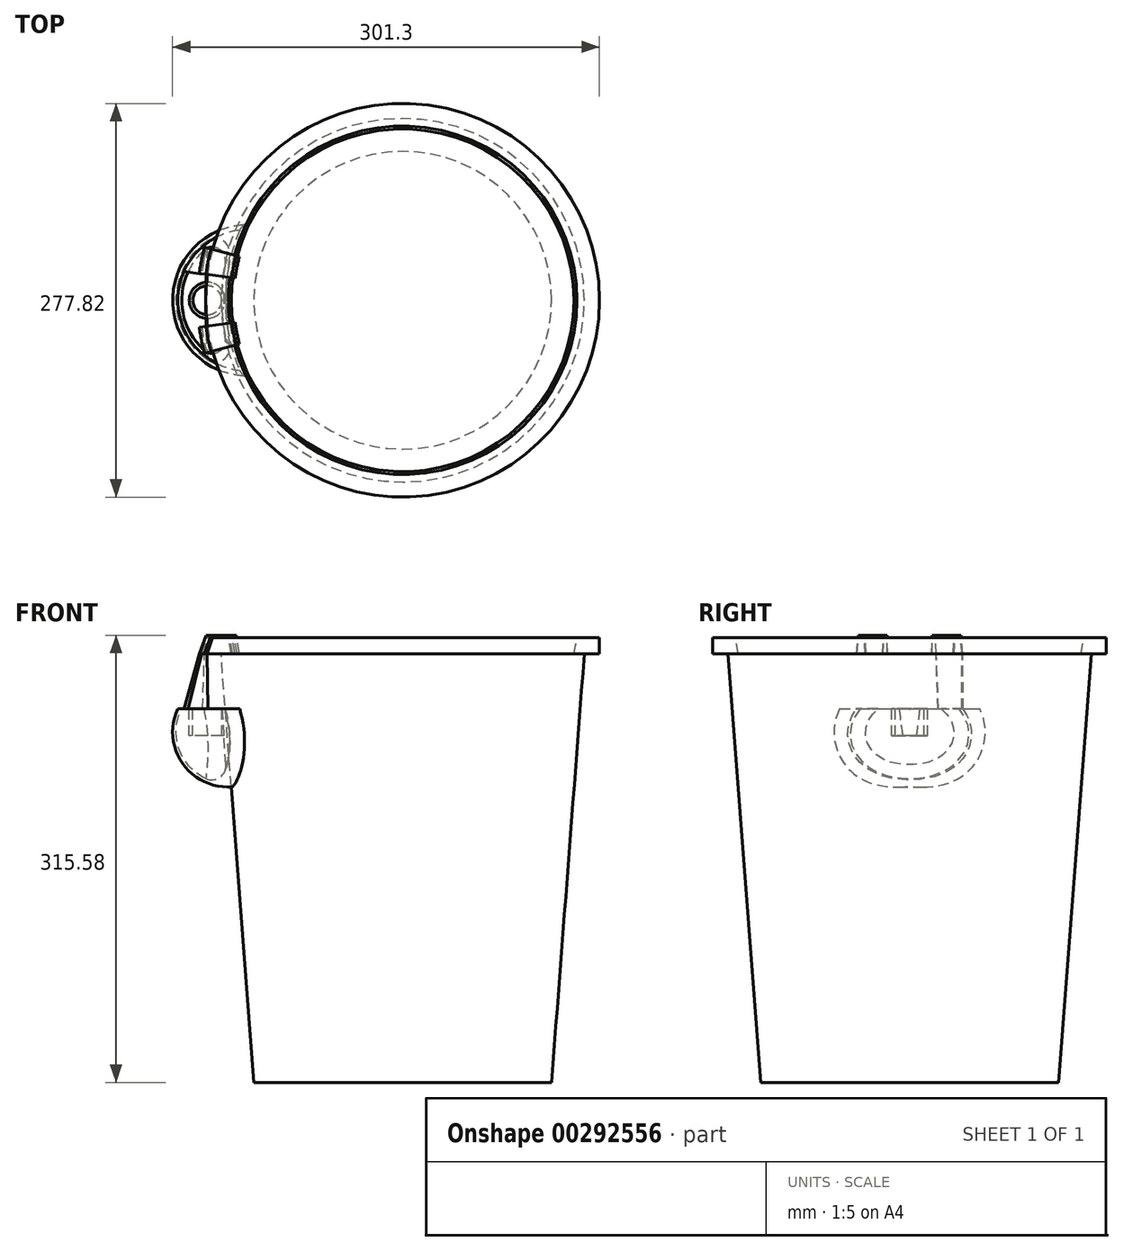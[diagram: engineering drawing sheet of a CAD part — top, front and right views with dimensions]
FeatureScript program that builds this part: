
annotation { "Feature Type Name" : "Feature", "Feature Type Description" : "" }
export const myFeature = defineFeature(function(context is Context, id is Id, definition is map)
    precondition{}
    {
        {
            var Q0;
            Q0=qCreatedBy(makeId("Front.planeOp"),FACE);
            var sketch = newSketch(context, id + "F0", { "sketchPlane" : qUnion([Q0])});
            skLineSegment(sketch, "E0", {"start": v(0, 0) * mm, "end": v(-105.1, 0) * mm});
            skLineSegment(sketch, "E1", {"start": v(-105.1, 0) * mm, "end": v(-128.2, 302.33) * mm});
            skLineSegment(sketch, "E2", {"start": v(-128.2, 302.33) * mm, "end": v(0, 302.33) * mm});
            skLineSegment(sketch, "E3", {"start": v(0, 302.33) * mm, "end": v(0, 0) * mm});
            skLineSegment(sketch, "E4.MirrorCS", {"start": v(128.2, 302.33) * mm, "end": v(0, 302.33) * mm, "construction": true});
            skLineSegment(sketch, "E5.MirrorCS", {"start": v(105.1, 0) * mm, "end": v(128.2, 302.33) * mm});
            skLineSegment(sketch, "E6.MirrorCS", {"start": v(0, 0) * mm, "end": v(105.1, 0) * mm});
            skArc(sketch, "E7", {"start": v(-138.8, 282.91) * mm, "mid": v(-150.57, 275.12) * mm, "end": v(-158.77, 263.61) * mm});
            skLineSegment(sketch, "E8", {"start": v(-125.23, 263.61) * mm, "end": v(-158.77, 263.61) * mm});
            skArc(sketch, "E9", {"start": v(-158.77, 263.61) * mm, "mid": v(-155.6, 225.36) * mm, "end": v(-121.04, 208.66) * mm});
            skLineSegment(sketch, "E10", {"start": v(-121.04, 208.66) * mm, "end": v(-121.04, 269.89) * mm, "construction": true});
            skLineSegment(sketch, "E11", {"start": v(-108.91, 147.35) * mm, "end": v(-108.91, 247.43) * mm});
            skLineSegment(sketch, "E12.bottom", {"start": v(-120.9, 302.33) * mm, "end": v(-138.9, 302.33) * mm});
            skLineSegment(sketch, "E12.top", {"start": v(-123, 313.98) * mm, "end": v(-138.9, 313.98) * mm});
            skLineSegment(sketch, "E12.left", {"start": v(-120.9, 302.33) * mm, "end": v(-123, 313.98) * mm});
            skLineSegment(sketch, "E12.right", {"start": v(-138.9, 302.33) * mm, "end": v(-138.9, 313.98) * mm});
            skLineSegment(sketch, "E13.MirrorCS", {"start": v(120.9, 302.33) * mm, "end": v(123, 313.98) * mm});
            skLineSegment(sketch, "E14.MirrorCS", {"start": v(123, 313.98) * mm, "end": v(138.9, 313.98) * mm});
            skLineSegment(sketch, "E15.MirrorCS", {"start": v(138.9, 302.33) * mm, "end": v(138.9, 313.98) * mm});
            skLineSegment(sketch, "E16.MirrorCS", {"start": v(120.9, 302.33) * mm, "end": v(138.9, 302.33) * mm});
            skSolve(sketch);
        }
        {
            var Q0;
            {var subQ4=sQuery(id+"F0.wireOp",EDGE,"E0");Q0=makeQuery(id+"F0.imprint","IMPRINT",FACE,{"disambiguationData":[TD([[makeQuery(id+"F0.imprint","IMPRINT",EDGE,{"derivedFrom":subQ4}),-1.0]])]});}
            var Q1;
            Q1=makeQuery(id+"F0.imprint","IMPRINT",FACE,{"disambiguationData":[TD([[makeQuery(id+"F0.imprint","IMPRINT",EDGE,{"derivedFrom":sQuery(id+"F0.wireOp",EDGE,"E12.top")}),1.0]])]});
            var Q2;
            Q2=sQuery(id+"F0.wireOp",EDGE,"E3");
            revolve(context, id + "F1", {"entities" : qUnion([Q0, Q1]), "axis" : qUnion([Q2]), "revolveType" : RevolveType.FULL});
        }
        {
            var Q0;
            {var subQ0=sQuery(id+"F0.wireOp",EDGE,"E8");Q0=makeQuery(id+"F0.imprint","IMPRINT",FACE,{"disambiguationData":[TD([[makeQuery(id+"F0.imprint","IMPRINT",EDGE,{"derivedFrom":subQ0}),1.0]])]});}
            var Q1;
            Q1=sQuery(id+"F0.wireOp",EDGE,"E11");
            revolve(context, id + "F2", {"entities" : qUnion([Q0]), "axis" : qUnion([Q1]), "revolveType" : RevolveType.FULL});
        }
        {
            var Q0;
            Q0=makeQuery(id+"F1.opRevolve","SWEPT_BODY",BODY,{"disambiguationData":[OSD([sQuery(id+"F0.wireOp",EDGE,"E0"),sQuery(id+"F0.wireOp",EDGE,"E1"),sQuery(id+"F0.wireOp",EDGE,"E2"),sQuery(id+"F0.wireOp",EDGE,"E3")])]});
            var Q1;
            Q1=makeQuery(id+"F2.opRevolve","SWEPT_BODY",BODY,{"disambiguationData":[OSD([sQuery(id+"F0.wireOp",EDGE,"E1"),sQuery(id+"F0.wireOp",EDGE,"E8"),sQuery(id+"F0.wireOp",EDGE,"E9")])]});
            booleanBodies(context, id + "F3", {"operationType" : BooleanOperationType.SUBTRACTION, "tools" : qUnion([Q0]), "targets" : qUnion([Q1]), "keepTools" : true});
        }
        {
            var Q0;
            Q0=makeQuery(id+"F2.opRevolve","SWEPT_FACE",FACE,{"disambiguationData":[OSD([sQuery(id+"F0.wireOp",EDGE,"E8")])]});
            shell(context, id + "F4", {"entities" : qUnion([Q0]), "thickness" : 2.5 * mm});
        }
        {
            var Q0;
            Q0=makeQuery(id+"F2.opRevolve","SWEPT_FACE",FACE,{"disambiguationData":[OSD([sQuery(id+"F0.wireOp",EDGE,"E8")])]});
            var sketch = newSketch(context, id + "F5", { "sketchPlane" : qUnion([Q0])});
            skCircle(sketch, "E17", {"center": v(-137.93, 0) * mm, "radius": 12.7 * mm});
            skSolve(sketch);
        }
        {
            var Q0;
            {var subQ0=sQuery(id+"F5.wireOp",EDGE,"E17");var subQ1=makeQuery(id+"F4.opShell","OFFSET_EDGE",EDGE,{"disambiguationData":[OSD([sQuery(id+"F0.wireOp",EDGE,"E1"),sQuery(id+"F0.wireOp",EDGE,"E8")])]});var subQ2=makeQuery(id+"F5.imprint","INTERSECT",VERTEX,{"disambiguationData":[OD(0.0)],"derivedFrom":[subQ1,subQ0]});Q0=makeQuery(id+"F5.imprint","IMPRINT",FACE,{"disambiguationData":[TD([[makeQuery(id+"F5.imprint","IMPRINT",EDGE,{"disambiguationData":[TD([[subQ2,-1.0]])],"derivedFrom":subQ0}),1.0]])]});}
            var Q1;
            {var subQ0=sQuery(id+"F5.wireOp",EDGE,"E17");var subQ1=sQuery(id+"F0.wireOp",EDGE,"E8");var subQ2=sQuery(id+"F0.wireOp",EDGE,"E1");var subQ3=makeQuery(id+"F5.imprint","INTERSECT",VERTEX,{"derivedFrom":[makeQuery(id+"F3.opBoolean","INTERSECT",EDGE,{"derivedFrom":[makeQuery(id+"F1.opRevolve","SWEPT_FACE",FACE,{"disambiguationData":[OSD([subQ2])]}),makeQuery(id+"F2.opRevolve","SWEPT_FACE",FACE,{"disambiguationData":[OSD([subQ1])]})]}),subQ0]});Q1=makeQuery(id+"F5.imprint","IMPRINT",FACE,{"disambiguationData":[TD([[makeQuery(id+"F5.imprint","IMPRINT",EDGE,{"disambiguationData":[TD([[subQ3,-1.0]])],"derivedFrom":subQ0}),1.0]])]});}
            extrude(context, id + "F6", {"entities" : qUnion([Q0, Q1]), "oppositeDirection" : true, "depth" : 18.98 * mm});
        }
        {
            var Q0;
            Q0=makeQuery(id+"F6.opExtrude","CAP_FACE",FACE,{"disambiguationData":[OSD([sQuery(id+"F5.wireOp",EDGE,"E17")])],"isStart":true});
            var Q1;
            Q1=makeQuery(id+"F6.opExtrude","CAP_FACE",FACE,{"disambiguationData":[OSD([sQuery(id+"F5.wireOp",EDGE,"E17")])],"isStart":false});
            shell(context, id + "F7", {"entities" : qUnion([Q0, Q1]), "thickness" : 2.5 * mm});
        }
        {
            var Q0;
            Q0=makeQuery(id+"F2.opRevolve","SWEPT_BODY",BODY,{"disambiguationData":[OSD([sQuery(id+"F0.wireOp",EDGE,"E1"),sQuery(id+"F0.wireOp",EDGE,"E8"),sQuery(id+"F0.wireOp",EDGE,"E9")])]});
            var Q1;
            Q1=makeQuery(id+"F6.opExtrude","SWEPT_BODY",BODY,{"disambiguationData":[OSD([sQuery(id+"F5.wireOp",EDGE,"E17")])]});
            booleanBodies(context, id + "F8", {"operationType" : BooleanOperationType.UNION, "tools" : qUnion([Q0, Q1])});
        }
        {
            var Q0;
            Q0=makeQuery(id+"F4.opShell","OFFSET_EDGE",EDGE,{"disambiguationData":[OSD([sQuery(id+"F0.wireOp",EDGE,"E1"),sQuery(id+"F0.wireOp",EDGE,"E9")])]});
            fillet(context, id + "F9", {"entities" : qUnion([Q0]), "radius" : 10 * mm, "tangentPropagation" : true, "allowEdgeOverflow" : false});
        }
        {
            var Q0;
            Q0=qCreatedBy(makeId("Front.planeOp"),FACE);
            var sketch = newSketch(context, id + "F10", { "sketchPlane" : qUnion([Q0])});
            skLineSegment(sketch, "E18.0.0", {"start": v(-121.04, 208.66) * mm, "end": v(-125.23, 263.61) * mm});
            skLineSegment(sketch, "E18.0.1", {"start": v(-125.23, 263.61) * mm, "end": v(-158.77, 263.61) * mm});
            skArc(sketch, "E18.0.2", {"start": v(-158.77, 263.61) * mm, "mid": v(-155.6, 225.36) * mm, "end": v(-121.04, 208.66) * mm});
            skLineSegment(sketch, "E19.0.0", {"start": v(-128.2, 302.33) * mm, "end": v(-120.9, 302.33) * mm});
            skLineSegment(sketch, "E19.0.1", {"start": v(-120.9, 302.33) * mm, "end": v(-123, 313.98) * mm});
            skLineSegment(sketch, "E19.0.2", {"start": v(-123, 313.98) * mm, "end": v(-138.9, 313.98) * mm});
            skLineSegment(sketch, "E19.0.3", {"start": v(-138.9, 313.98) * mm, "end": v(-138.9, 302.33) * mm});
            skLineSegment(sketch, "E19.0.4", {"start": v(-138.9, 302.33) * mm, "end": v(-128.2, 302.33) * mm});
            skLineSegment(sketch, "E20.0", {"start": v(0, 302.33) * mm, "end": v(0, 0) * mm});
            skLineSegment(sketch, "E21.1", {"start": v(-121.67, 315.58) * mm, "end": v(-140.03, 315.58) * mm});
            skLineSegment(sketch, "E21.2", {"start": v(-119.33, 302.62) * mm, "end": v(-121.67, 315.58) * mm});
            skLineSegment(sketch, "E22", {"start": v(-120.9, 302.33) * mm, "end": v(-119.33, 302.62) * mm});
            skLineSegment(sketch, "E23", {"start": v(-158.77, 263.61) * mm, "end": v(-140.03, 315.58) * mm});
            skLineSegment(sketch, "E24.0", {"start": v(-157.21, 263.23) * mm, "end": v(-138.9, 313.98) * mm});
            skLineSegment(sketch, "E25", {"start": v(-143.1, 302.33) * mm, "end": v(-144.8, 302.33) * mm});
            skSolve(sketch);
        }
        {
            var Q0;
            Q0=makeQuery(id+"F10.imprint","IMPRINT",FACE,{"disambiguationData":[TD([[makeQuery(id+"F10.imprint","IMPRINT",EDGE,{"derivedFrom":sQuery(id+"F10.wireOp",EDGE,"E19.0.1")}),-1.0]])]});
            var Q1;
            Q1=sQuery(id+"F10.wireOp",EDGE,"E20.0");
            revolve(context, id + "F11", {"entities" : qUnion([Q0]), "axis" : qUnion([Q1]), "revolveType" : RevolveType.SYMMETRIC, "angle" : 30 * degree});
        }
        {
            var Q0;
            Q0=makeQuery(id+"F10.imprint","IMPRINT",FACE,{"disambiguationData":[TD([[makeQuery(id+"F10.imprint","IMPRINT",EDGE,{"derivedFrom":sQuery(id+"F10.wireOp",EDGE,"E19.0.1")}),-1.0]])]});
            var Q1;
            Q1=sQuery(id+"F0.wireOp",EDGE,"E3");
            revolve(context, id + "F12", {"operationType" : NewBodyOperationType.REMOVE, "entities" : qUnion([Q0]), "axis" : qUnion([Q1]), "revolveType" : RevolveType.SYMMETRIC, "oppositeDirection" : true, "angle" : 15 * degree});
        }
        {
            var Q0;
            Q0=makeQuery(id+"F8.opBoolean","MERGE",FACE,{"derivedFrom":[makeQuery(id+"F2.opRevolve","SWEPT_FACE",FACE,{"disambiguationData":[OSD([sQuery(id+"F0.wireOp",EDGE,"E8")])]}),makeQuery(id+"F6.opExtrude","CAP_FACE",FACE,{"disambiguationData":[OSD([sQuery(id+"F5.wireOp",EDGE,"E17")])],"isStart":true})]});
            var sketch = newSketch(context, id + "F13", { "sketchPlane" : qUnion([Q0])});
            skLineSegment(sketch, "E26", {"start": v(-151.56, 19.95) * mm, "end": v(-154.44, 20.33) * mm});
            skArc(sketch, "E27.0", {"start": v(-154.44, 20.33) * mm, "mid": v(-148.87, 29.83) * mm, "end": v(-141.34, 37.87) * mm});
            skArc(sketch, "E28.0", {"start": v(-151.56, 19.95) * mm, "mid": v(-146.76, 28.01) * mm, "end": v(-140.45, 34.96) * mm});
            skFitSpline(sketch, "E29.0", {"points": [v(-140.45, 34.96) * mm, v(-140.03, 35.34) * mm, v(-139.36, 35.86) * mm, v(-138.4, 36.45) * mm, v(-137.63, 36.83) * mm, v(-136.84, 37.14) * mm, v(-136.03, 37.38) * mm, v(-135.2, 37.53) * mm, v(-134.5, 37.6) * mm, v(-133.92, 37.6) * mm, v(-133.35, 37.57) * mm, v(-132.65, 37.49) * mm, v(-131.83, 37.3) * mm, v(-131.02, 37) * mm, v(-130.25, 36.64) * mm, v(-129.53, 36.2) * mm, v(-128.85, 35.66) * mm, v(-128.23, 35.07) * mm, v(-127.68, 34.43) * mm, v(-127.18, 33.73) * mm, v(-126.75, 33) * mm, v(-126.39, 32.22) * mm, v(-126.08, 31.43) * mm, v(-125.75, 30.33) * mm, v(-125.48, 28.95) * mm, v(-125.35, 27.26) * mm, v(-125.38, 25.55) * mm, v(-125.53, 23.86) * mm, v(-125.7, 22.74) * mm, v(-125.8, 22.18) * mm]});
            skLineSegment(sketch, "E30", {"start": v(-141.34, 37.87) * mm, "end": v(-137.54, 36.85) * mm});
            skPoint(sketch, "E31.orphan", {"position": v(-125.8, 22.18) * mm});
            skPoint(sketch, "E32.orphan", {"position": v(-115.04, 49.48) * mm});
            skPoint(sketch, "E33.orphan", {"position": v(-115.04, -49.48) * mm});
            skPoint(sketch, "E34.orphan", {"position": v(-140.45, -34.96) * mm});
            skSolve(sketch);
        }
        {
            var Q1;
            {var subQ0=sQuery(id+"F0.wireOp",EDGE,"E8");var subQ1=sQuery(id+"F0.wireOp",EDGE,"E9");var subQ5=sQuery(id+"F13.wireOp",EDGE,"E26");var subQ8=makeQuery(id+"F2.opRevolve","SWEPT_EDGE",EDGE,{"disambiguationData":[OSD([subQ0,subQ1])]});var subQ11=makeQuery(id+"F13.imprint","INTERSECT",VERTEX,{"derivedFrom":[subQ8,subQ5]});Q1=makeQuery(id+"F13.imprint","IMPRINT",FACE,{"disambiguationData":[TD([[makeQuery(id+"F13.imprint","IMPRINT",EDGE,{"disambiguationData":[TD([[subQ11,1.0]])],"derivedFrom":subQ5}),-1.0]])]});}
            var Q2;
            {var subQ0=sQuery(id+"F10.wireOp",EDGE,"E25");var subQ1=sQuery(id+"F10.wireOp",EDGE,"E24.0");var subQ2=sQuery(id+"F10.wireOp",EDGE,"E23");var subQ3=sQuery(id+"F10.wireOp",EDGE,"E22");var subQ4=sQuery(id+"F10.wireOp",EDGE,"E21.2");var subQ5=sQuery(id+"F10.wireOp",EDGE,"E21.1");var subQ6=sQuery(id+"F10.wireOp",EDGE,"E19.0.2");var subQ7=sQuery(id+"F10.wireOp",EDGE,"E19.0.1");Q2=makeQuery(id+"F12.boolean.opBoolean","SPLIT",FACE,{"disambiguationData":[TD([makeQuery(id+"F11.opRevolve","CAP_FACE",FACE,{"disambiguationData":[OSD([subQ7,subQ6,subQ5,subQ4,subQ3,subQ2,subQ1,subQ0])],"isStart":false})])],"derivedFrom":makeQuery(id+"F11.opRevolve","SWEPT_FACE",FACE,{"disambiguationData":[OSD([subQ0])]})});}
            var Q3;
            Q3=sQuery(id+"F13.wireOp",VERTEX,"E30.start");
            var Q4;
            Q4=makeQuery(id+"F11.opRevolve","CAP_VERTEX",VERTEX,{"disambiguationData":[OSD([sQuery(id+"F10.wireOp",EDGE,"E23"),sQuery(id+"F10.wireOp",EDGE,"E25")])],"isStart":false});
            loft(context, id + "F14", {"operationType" : NewBodyOperationType.ADD, "sheetProfilesArray" : [{ "sheetProfileEntities" : qUnion([Q1]) }, { "sheetProfileEntities" : qUnion([Q2]) }], "matchConnections" : true, "connections" : [{ "connectionEntities" : qUnion([Q3, Q4]), "connectionEdgeQueries" : qUnion([]), "connectionEdgeParameters" : [] }]});
        }
    });
